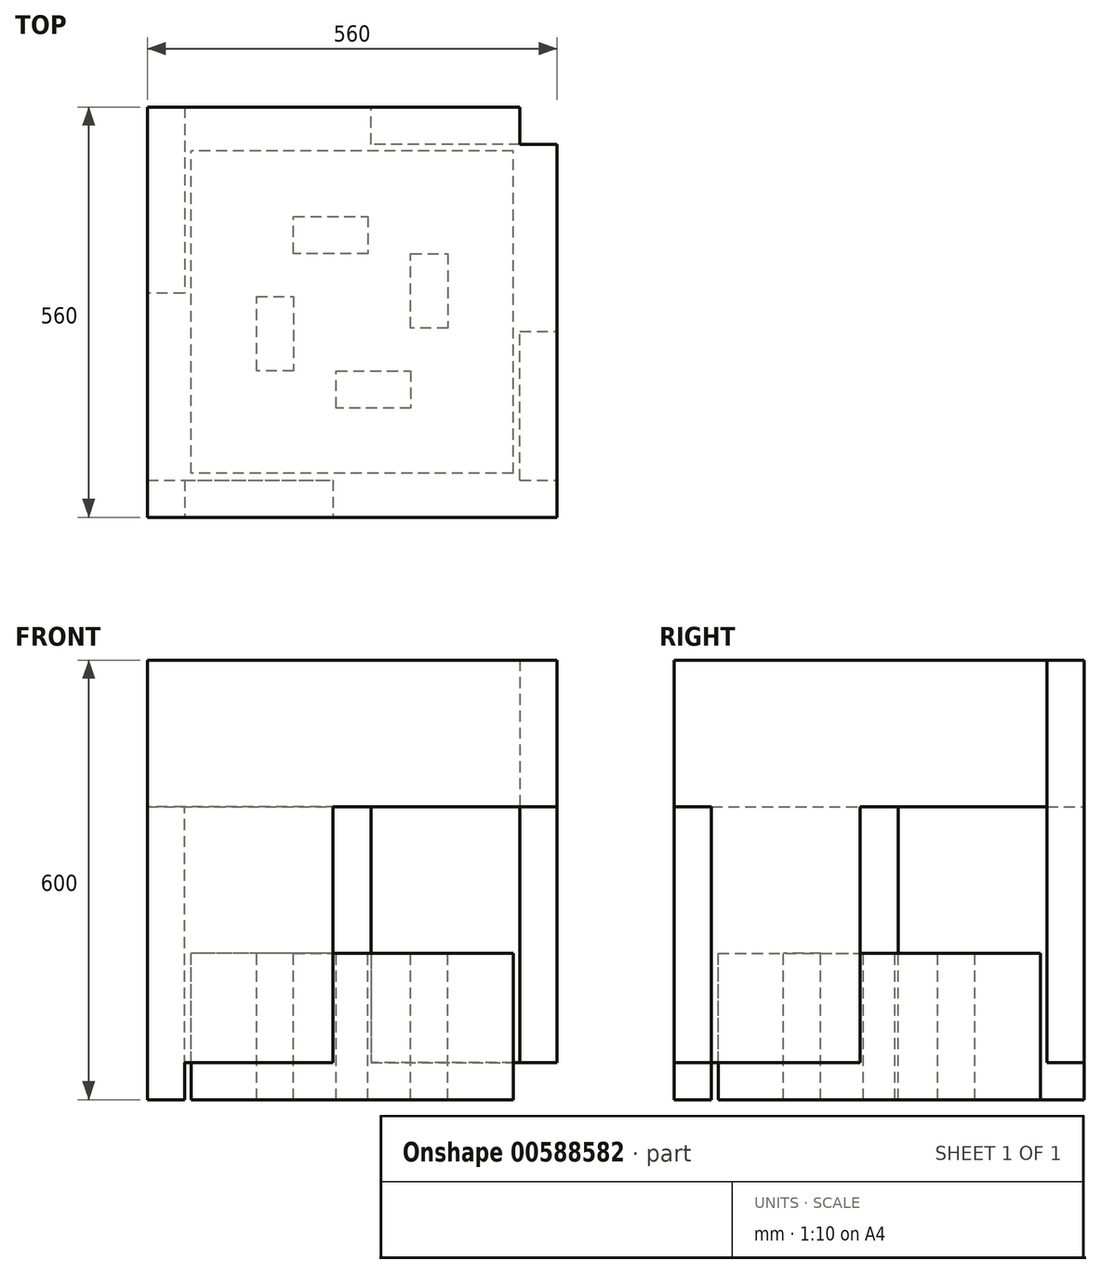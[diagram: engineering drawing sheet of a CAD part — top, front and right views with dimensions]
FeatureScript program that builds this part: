
annotation { "Feature Type Name" : "Feature", "Feature Type Description" : "" }
export const myFeature = defineFeature(function(context is Context, id is Id, definition is map)
    precondition{}
    {
        {
            var Q0;
            Q0=qCreatedBy(makeId("Top.planeOp"),FACE);
            var sketch = newSketch(context, id + "F0", { "sketchPlane" : qUnion([Q0])});
            skLineSegment(sketch, "E0.bottom", {"start": v(-214.26, 289.89) * mm, "end": v(345.74, 289.89) * mm});
            skLineSegment(sketch, "E0.top", {"start": v(-214.26, -270.11) * mm, "end": v(345.74, -270.11) * mm});
            skLineSegment(sketch, "E0.left", {"start": v(-214.26, 289.89) * mm, "end": v(-214.26, -270.11) * mm});
            skLineSegment(sketch, "E0.right", {"start": v(345.74, 289.89) * mm, "end": v(345.74, -270.11) * mm});
            skLineSegment(sketch, "E1", {"start": v(-14.26, 89.89) * mm, "end": v(-14.26, 140.69) * mm});
            skLineSegment(sketch, "E2", {"start": v(-14.26, 140.69) * mm, "end": v(87.34, 140.69) * mm});
            skLineSegment(sketch, "E3", {"start": v(87.34, 140.69) * mm, "end": v(87.34, 89.89) * mm});
            skLineSegment(sketch, "E4", {"start": v(87.34, 89.89) * mm, "end": v(-14.26, 89.89) * mm});
            skLineSegment(sketch, "E5", {"start": v(145.74, 89.89) * mm, "end": v(196.54, 89.89) * mm});
            skLineSegment(sketch, "E6", {"start": v(196.54, 89.89) * mm, "end": v(196.54, -11.71) * mm});
            skLineSegment(sketch, "E7", {"start": v(145.74, -70.11) * mm, "end": v(145.74, -120.91) * mm});
            skLineSegment(sketch, "E8", {"start": v(145.74, -120.91) * mm, "end": v(44.14, -120.91) * mm});
            skLineSegment(sketch, "E9", {"start": v(-14.26, -70.11) * mm, "end": v(-65.06, -70.11) * mm});
            skLineSegment(sketch, "E10", {"start": v(-65.06, -70.11) * mm, "end": v(-65.06, 31.49) * mm});
            skLineSegment(sketch, "E11", {"start": v(-65.06, 31.49) * mm, "end": v(-14.26, 31.49) * mm});
            skLineSegment(sketch, "E12", {"start": v(-14.26, 31.49) * mm, "end": v(-14.26, -70.11) * mm});
            skLineSegment(sketch, "E13", {"start": v(44.14, -120.91) * mm, "end": v(44.14, -70.11) * mm});
            skLineSegment(sketch, "E14", {"start": v(44.14, -70.11) * mm, "end": v(145.74, -70.11) * mm});
            skLineSegment(sketch, "E15", {"start": v(196.54, -11.71) * mm, "end": v(145.74, -11.71) * mm});
            skLineSegment(sketch, "E16", {"start": v(145.74, -11.71) * mm, "end": v(145.74, 89.89) * mm});
            skLineSegment(sketch, "E17", {"start": v(-214.26, 289.89) * mm, "end": v(-163.46, 289.89) * mm});
            skLineSegment(sketch, "E18", {"start": v(-163.46, 289.89) * mm, "end": v(-163.46, 239.09) * mm});
            skLineSegment(sketch, "E19", {"start": v(-163.46, 239.09) * mm, "end": v(-214.26, 239.09) * mm});
            skLineSegment(sketch, "E20", {"start": v(-214.26, 239.09) * mm, "end": v(-214.26, 289.89) * mm});
            skLineSegment(sketch, "E21", {"start": v(-163.46, 239.09) * mm, "end": v(-163.46, 35.89) * mm});
            skLineSegment(sketch, "E22", {"start": v(-163.46, 35.89) * mm, "end": v(-214.26, 35.89) * mm});
            skLineSegment(sketch, "E23", {"start": v(-214.26, 35.89) * mm, "end": v(-214.26, 239.09) * mm});
            skLineSegment(sketch, "E24", {"start": v(-214.26, -270.11) * mm, "end": v(-214.26, -219.31) * mm});
            skLineSegment(sketch, "E25", {"start": v(-214.26, -219.31) * mm, "end": v(-163.46, -219.31) * mm});
            skLineSegment(sketch, "E26", {"start": v(-163.46, -219.31) * mm, "end": v(-163.46, -270.11) * mm});
            skLineSegment(sketch, "E27", {"start": v(-163.46, -270.11) * mm, "end": v(-214.26, -270.11) * mm});
            skLineSegment(sketch, "E28", {"start": v(-163.46, -219.31) * mm, "end": v(39.74, -219.31) * mm});
            skLineSegment(sketch, "E29", {"start": v(39.74, -219.31) * mm, "end": v(39.74, -270.11) * mm});
            skLineSegment(sketch, "E30", {"start": v(294.94, -270.11) * mm, "end": v(294.94, -219.31) * mm});
            skLineSegment(sketch, "E31", {"start": v(294.94, -219.31) * mm, "end": v(345.74, -219.31) * mm});
            skLineSegment(sketch, "E32", {"start": v(345.74, -219.31) * mm, "end": v(345.74, -270.11) * mm});
            skLineSegment(sketch, "E33", {"start": v(294.94, -219.31) * mm, "end": v(294.94, -16.11) * mm});
            skLineSegment(sketch, "E34", {"start": v(294.94, -16.11) * mm, "end": v(345.74, -16.11) * mm});
            skLineSegment(sketch, "E35", {"start": v(345.74, -16.11) * mm, "end": v(345.74, -219.31) * mm});
            skLineSegment(sketch, "E36", {"start": v(294.94, 289.89) * mm, "end": v(294.94, 239.09) * mm});
            skLineSegment(sketch, "E37", {"start": v(294.94, 239.09) * mm, "end": v(345.74, 239.09) * mm});
            skLineSegment(sketch, "E38", {"start": v(294.94, 239.09) * mm, "end": v(91.74, 239.09) * mm});
            skLineSegment(sketch, "E39", {"start": v(91.74, 239.09) * mm, "end": v(91.74, 289.89) * mm});
            skLineSegment(sketch, "E40.top", {"start": v(-65.06, 140.69) * mm, "end": v(-14.26, 140.69) * mm});
            skLineSegment(sketch, "E40.left", {"start": v(-65.06, 31.49) * mm, "end": v(-65.06, 140.69) * mm});
            skLineSegment(sketch, "E41.bottom", {"start": v(145.74, -120.91) * mm, "end": v(196.54, -120.91) * mm});
            skLineSegment(sketch, "E41.top", {"start": v(145.74, -11.71) * mm, "end": v(196.54, -11.71) * mm});
            skLineSegment(sketch, "E41.right", {"start": v(196.54, -120.91) * mm, "end": v(196.54, -11.71) * mm});
            skLineSegment(sketch, "E42.bottom", {"start": v(196.54, -120.91) * mm, "end": v(-65.06, -120.91) * mm});
            skLineSegment(sketch, "E42.top", {"start": v(196.54, 140.69) * mm, "end": v(-65.06, 140.69) * mm});
            skLineSegment(sketch, "E42.left", {"start": v(196.54, -120.91) * mm, "end": v(196.54, 140.69) * mm});
            skLineSegment(sketch, "E42.right", {"start": v(-65.06, -120.91) * mm, "end": v(-65.06, 140.69) * mm});
            skLineSegment(sketch, "E43.left", {"start": v(-154.26, -210.11) * mm, "end": v(-154.26, 229.89) * mm});
            skLineSegment(sketch, "E43.right", {"start": v(285.74, -210.11) * mm, "end": v(285.74, 229.89) * mm});
            skPoint(sketch, "E44", {"position": v(-154.26, 9.89) * mm});
            skLineSegment(sketch, "E45", {"start": v(285.74, -210.11) * mm, "end": v(-154.26, -210.11) * mm});
            skLineSegment(sketch, "E46", {"start": v(285.74, 229.89) * mm, "end": v(-154.26, 229.89) * mm});
            skPoint(sketch, "E47", {"position": v(65.74, 229.89) * mm});
            skPoint(sketch, "E48", {"position": v(285.74, 9.89) * mm});
            skPoint(sketch, "E49", {"position": v(65.74, -210.11) * mm});
            skSolve(sketch);
        }
        {
            var Q0;
            Q0=makeQuery(id+"F0.imprint","IMPRINT",FACE,{"disambiguationData":[TD([[makeQuery(id+"F0.imprint","IMPRINT",EDGE,{"derivedFrom":sQuery(id+"F0.wireOp",EDGE,"E0.left")}),1.0]])]});
            var Q1;
            {var subQ17=sQuery(id+"F0.wireOp",EDGE,"E43.bottom");var subQ19=makeQuery(id+"F0.imprint","IMPRINT",VERTEX,{"derivedFrom":subQ17});Q1=makeQuery(id+"F0.imprint","IMPRINT",FACE,{"disambiguationData":[TD([[makeQuery(id+"F0.imprint","IMPRINT",EDGE,{"disambiguationData":[TD([[subQ19,1.0]])],"derivedFrom":subQ17}),1.0]])]});}
            var Q2;
            {var subQ3=sQuery(id+"F0.wireOp",EDGE,"E1");Q2=makeQuery(id+"F0.imprint","IMPRINT",FACE,{"disambiguationData":[TD([[makeQuery(id+"F0.imprint","IMPRINT",EDGE,{"derivedFrom":subQ3}),1.0]])]});}
            var Q3;
            Q3=makeQuery(id+"F0.imprint","IMPRINT",FACE,{"disambiguationData":[TD([[makeQuery(id+"F0.imprint","IMPRINT",EDGE,{"derivedFrom":sQuery(id+"F0.wireOp",EDGE,"E43.left")}),-1.0]])]});
            extrude(context, id + "F1", {"entities" : qUnion([Q0, Q1, Q2, Q3]), "depth" : -50.8 * mm, "offsetDistance" : 25 * mm});
        }
        {
            var Q0;
            Q0=makeQuery(id+"F0.imprint","IMPRINT",FACE,{"disambiguationData":[TD([[makeQuery(id+"F0.imprint","IMPRINT",EDGE,{"derivedFrom":sQuery(id+"F0.wireOp",EDGE,"E0.left")}),1.0]])]});
            var Q1;
            Q1=makeQuery(id+"F0.imprint","IMPRINT",FACE,{"disambiguationData":[TD([[makeQuery(id+"F0.imprint","IMPRINT",EDGE,{"derivedFrom":sQuery(id+"F0.wireOp",EDGE,"E31")}),1.0]])]});
            var Q2;
            {var subQ0=sQuery(id+"F0.wireOp",EDGE,"E36");Q2=makeQuery(id+"F0.imprint","IMPRINT",FACE,{"disambiguationData":[TD([[makeQuery(id+"F0.imprint","IMPRINT",EDGE,{"derivedFrom":subQ0}),-1.0]])]});}
            var Q3;
            Q3=makeQuery(id+"F0.imprint","IMPRINT",FACE,{"disambiguationData":[TD([[makeQuery(id+"F0.imprint","IMPRINT",EDGE,{"derivedFrom":sQuery(id+"F0.wireOp",EDGE,"E19")}),1.0]])]});
            var Q4;
            {var subQ0=sQuery(id+"F0.wireOp",EDGE,"E26");Q4=makeQuery(id+"F0.imprint","IMPRINT",FACE,{"disambiguationData":[TD([[makeQuery(id+"F0.imprint","IMPRINT",EDGE,{"derivedFrom":subQ0}),1.0]])]});}
            extrude(context, id + "F2", {"entities" : qUnion([Q0, Q1, Q2, Q3, Q4]), "operationType" : NewBodyOperationType.ADD, "depth" : 349.2 * mm, "offsetDistance" : 25 * mm});
        }
        {
            var Q0;
            {var subQ17=sQuery(id+"F0.wireOp",EDGE,"E43.bottom");var subQ19=makeQuery(id+"F0.imprint","IMPRINT",VERTEX,{"derivedFrom":subQ17});Q0=makeQuery(id+"F0.imprint","IMPRINT",FACE,{"disambiguationData":[TD([[makeQuery(id+"F0.imprint","IMPRINT",EDGE,{"disambiguationData":[TD([[subQ19,1.0]])],"derivedFrom":subQ17}),1.0]])]});}
            var Q1;
            {var subQ3=sQuery(id+"F0.wireOp",EDGE,"E1");Q1=makeQuery(id+"F0.imprint","IMPRINT",FACE,{"disambiguationData":[TD([[makeQuery(id+"F0.imprint","IMPRINT",EDGE,{"derivedFrom":subQ3}),1.0]])]});}
            var Q2;
            Q2=makeQuery(id+"F0.imprint","IMPRINT",FACE,{"disambiguationData":[TD([[makeQuery(id+"F0.imprint","IMPRINT",EDGE,{"derivedFrom":sQuery(id+"F0.wireOp",EDGE,"E43.left")}),-1.0]])]});
            extrude(context, id + "F3", {"entities" : qUnion([Q0, Q1, Q2]), "operationType" : NewBodyOperationType.ADD, "depth" : 149.2 * mm, "offsetDistance" : 25 * mm});
        }
        {
            var Q0;
            Q0=makeQuery(id+"F2.opExtrude","CAP_FACE",FACE,{"disambiguationData":[OSD([sQuery(id+"F0.wireOp",EDGE,"E0.bottom"),sQuery(id+"F0.wireOp",EDGE,"E0.top"),sQuery(id+"F0.wireOp",EDGE,"E0.left"),sQuery(id+"F0.wireOp",EDGE,"E0.right"),sQuery(id+"F0.wireOp",EDGE,"E18"),sQuery(id+"F0.wireOp",EDGE,"E19"),sQuery(id+"F0.wireOp",EDGE,"E23"),sQuery(id+"F0.wireOp",EDGE,"E25"),sQuery(id+"F0.wireOp",EDGE,"E26"),sQuery(id+"F0.wireOp",EDGE,"E30"),sQuery(id+"F0.wireOp",EDGE,"E31"),sQuery(id+"F0.wireOp",EDGE,"E35"),sQuery(id+"F0.wireOp",EDGE,"E36"),sQuery(id+"F0.wireOp",EDGE,"E37"),sQuery(id+"F0.wireOp",EDGE,"E43.bottom"),sQuery(id+"F0.wireOp",EDGE,"E43.top"),sQuery(id+"F0.wireOp",EDGE,"E43.left"),sQuery(id+"F0.wireOp",EDGE,"E43.right")])],"isStart":false});
            var sketch = newSketch(context, id + "F4", { "sketchPlane" : qUnion([Q0])});
            skLineSegment(sketch, "E50.bottom", {"start": v(-163.46, -270.11) * mm, "end": v(-214.26, -270.11) * mm});
            skLineSegment(sketch, "E50.top", {"start": v(-163.46, -219.31) * mm, "end": v(-214.26, -219.31) * mm});
            skLineSegment(sketch, "E50.left", {"start": v(-163.46, -270.11) * mm, "end": v(-163.46, -219.31) * mm});
            skLineSegment(sketch, "E50.right", {"start": v(-214.26, -270.11) * mm, "end": v(-214.26, -219.31) * mm});
            skLineSegment(sketch, "E51.bottom", {"start": v(345.74, 239.09) * mm, "end": v(294.94, 239.09) * mm});
            skLineSegment(sketch, "E51.top", {"start": v(345.74, 289.89) * mm, "end": v(294.94, 289.89) * mm});
            skLineSegment(sketch, "E51.left", {"start": v(345.74, 239.09) * mm, "end": v(345.74, 289.89) * mm});
            skLineSegment(sketch, "E51.right", {"start": v(294.94, 239.09) * mm, "end": v(294.94, 289.89) * mm});
            skLineSegment(sketch, "E52.bottom", {"start": v(345.74, 289.89) * mm, "end": v(-214.26, 289.89) * mm});
            skLineSegment(sketch, "E52.top", {"start": v(345.74, -270.11) * mm, "end": v(-214.26, -270.11) * mm});
            skLineSegment(sketch, "E52.left", {"start": v(345.74, 289.89) * mm, "end": v(345.74, -270.11) * mm});
            skLineSegment(sketch, "E52.right", {"start": v(-214.26, 289.89) * mm, "end": v(-214.26, -270.11) * mm});
            skSolve(sketch);
        }
        {
            var Q0;
            {var subQ10=sQuery(id+"F4.wireOp",EDGE,"E50.top");Q0=makeQuery(id+"F4.imprint","IMPRINT",FACE,{"disambiguationData":[TD([[makeQuery(id+"F4.imprint","IMPRINT",EDGE,{"derivedFrom":subQ10}),1.0]])]});}
            var Q1;
            {var subQ0=sQuery(id+"F4.wireOp",EDGE,"E50.top");Q1=makeQuery(id+"F4.imprint","IMPRINT",FACE,{"disambiguationData":[TD([[makeQuery(id+"F4.imprint","IMPRINT",EDGE,{"derivedFrom":subQ0}),-1.0]])]});}
            var Q2;
            {var subQ0=sQuery(id+"F4.wireOp",EDGE,"E51.bottom");Q2=makeQuery(id+"F4.imprint","IMPRINT",FACE,{"disambiguationData":[TD([[makeQuery(id+"F4.imprint","IMPRINT",EDGE,{"derivedFrom":subQ0}),1.0]])]});}
            var Q3;
            {var subQ1=makeQuery(id+"F2.opExtrude","CAP_EDGE",EDGE,{"disambiguationData":[OSD([sQuery(id+"F0.wireOp",EDGE,"E18")])],"isStart":false});Q3=makeQuery(id+"F4.imprint","IMPRINT",FACE,{"disambiguationData":[TD([[makeQuery(id+"F4.imprint","IMPRINT",EDGE,{"derivedFrom":subQ1}),-1.0]])]});}
            var Q4;
            {var subQ1=makeQuery(id+"F2.opExtrude","CAP_EDGE",EDGE,{"disambiguationData":[OSD([sQuery(id+"F0.wireOp",EDGE,"E30")])],"isStart":false});Q4=makeQuery(id+"F4.imprint","IMPRINT",FACE,{"disambiguationData":[TD([[makeQuery(id+"F4.imprint","IMPRINT",EDGE,{"derivedFrom":subQ1}),-1.0]])]});}
            extrude(context, id + "F5", {"entities" : qUnion([Q0, Q1, Q2, Q3, Q4]), "operationType" : NewBodyOperationType.ADD, "depth" : 200 * mm, "offsetDistance" : 25 * mm});
        }
    });
